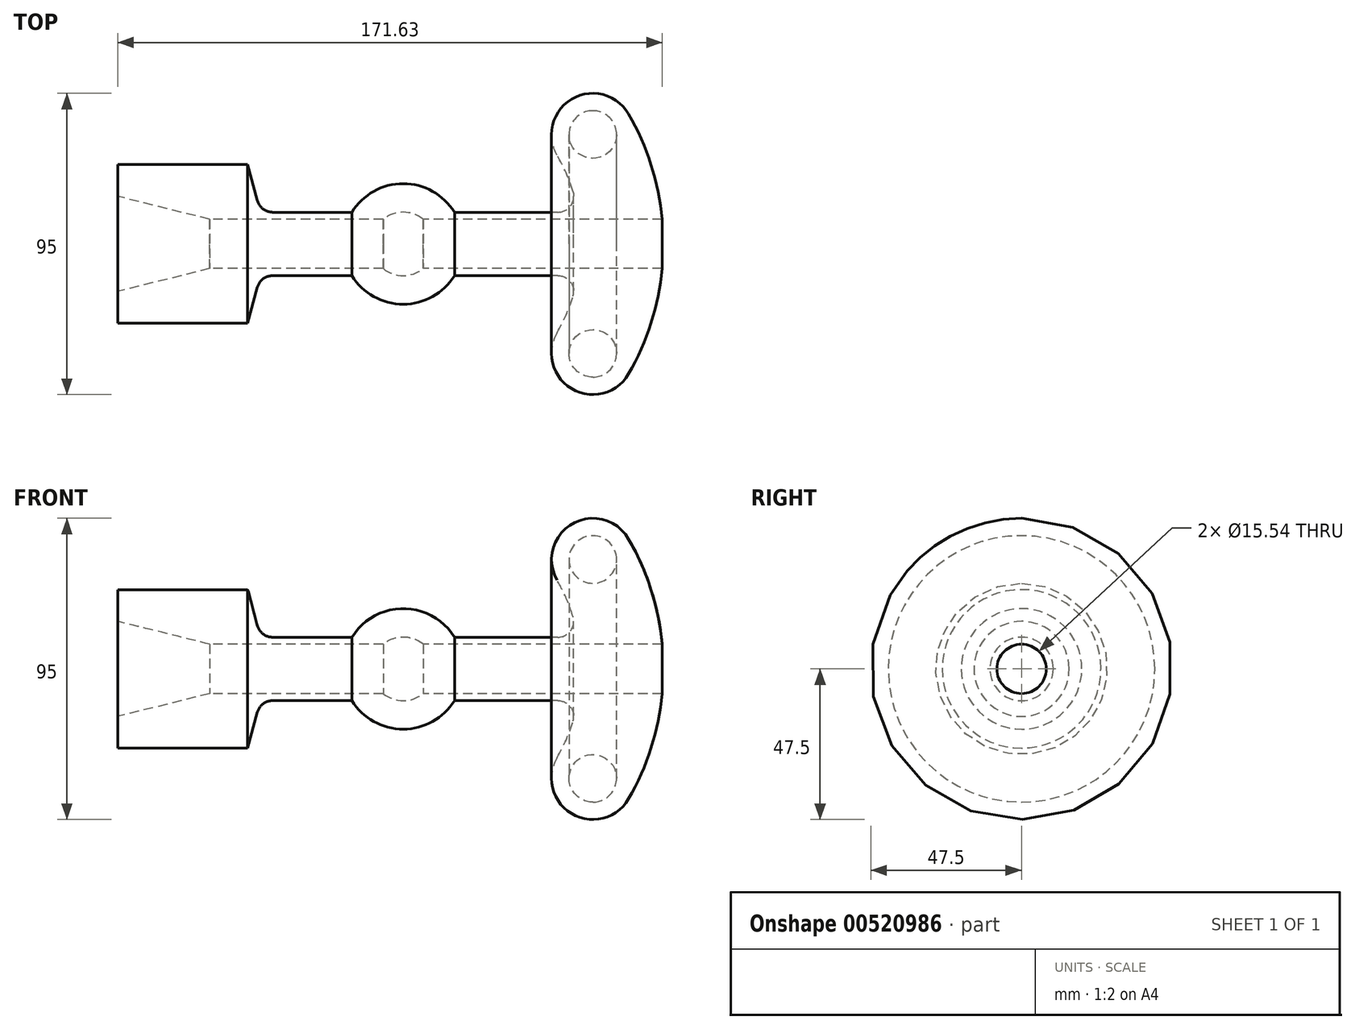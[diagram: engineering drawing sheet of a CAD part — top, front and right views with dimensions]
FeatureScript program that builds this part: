
annotation { "Feature Type Name" : "Feature", "Feature Type Description" : "" }
export const myFeature = defineFeature(function(context is Context, id is Id, definition is map)
    precondition{}
    {
        {
            var Q0;
            Q0=qCreatedBy(makeId("Front.planeOp"),FACE);
            var sketch = newSketch(context, id + "F0", { "sketchPlane" : qUnion([Q0])});
            skLineSegment(sketch, "E0", {"start": v(-90, 0) * mm, "end": v(69, 0) * mm, "construction": true});
            skArc(sketch, "E1", {"start": v(10, 0) * mm, "mid": v(0, 10) * mm, "end": v(-10, 0) * mm});
            skLineSegment(sketch, "E2", {"start": v(0, 0) * mm, "end": v(59.76, 34.5) * mm, "construction": true});
            skArc(sketch, "E3", {"start": v(69, 0) * mm, "mid": v(66.65, 17.86) * mm, "end": v(59.76, 34.5) * mm, "construction": true});
            skArc(sketch, "E4.0", {"start": v(82, 0) * mm, "mid": v(79.2, 21.22) * mm, "end": v(71.01, 41) * mm});
            skArc(sketch, "E5.0", {"start": v(55.1, 10) * mm, "mid": v(52.57, 19.28) * mm, "end": v(48.5, 28) * mm});
            skArc(sketch, "E6", {"start": v(71.01, 41) * mm, "mid": v(53.26, 45.76) * mm, "end": v(48.5, 28) * mm});
            skCircle(sketch, "E7", {"center": v(59.76, 34.5) * mm, "radius": 7.5 * mm});
            skLineSegment(sketch, "E8", {"start": v(0, 0) * mm, "end": v(56, 0) * mm, "construction": true});
            skArc(sketch, "E9", {"start": v(16.16, 10) * mm, "mid": v(0, 19) * mm, "end": v(-16.16, 10) * mm});
            skLineSegment(sketch, "E10.trimOffspring", {"start": v(16.16, 10) * mm, "end": v(55.1, 10) * mm});
            skLineSegment(sketch, "E11", {"start": v(-90, 25) * mm, "end": v(-90, 15) * mm});
            skLineSegment(sketch, "E12", {"start": v(-90, 25) * mm, "end": v(-49, 25) * mm});
            skLineSegment(sketch, "E13", {"start": v(-90, 15) * mm, "end": v(-61, 7.77) * mm});
            skLineSegment(sketch, "E14", {"start": v(0, 0) * mm, "end": v(-61, 0) * mm, "construction": true});
            skLineSegment(sketch, "E15", {"start": v(-61, 0) * mm, "end": v(-61, 7.77) * mm});
            skPoint(sketch, "E16.orphan", {"position": v(-90, 10) * mm});
            skLineSegment(sketch, "E17", {"start": v(-49, 25) * mm, "end": v(-44.98, 10) * mm});
            skLineSegment(sketch, "E18", {"start": v(-16.16, 10) * mm, "end": v(-44.98, 10) * mm});
            skLineSegment(sketch, "E19", {"start": v(-61, 0) * mm, "end": v(82, 0) * mm});
            skSolve(sketch);
        }
        {
            var Q0;
            {var subQ0=sQuery(id+"F0.wireOp",EDGE,"E1");Q0=makeQuery(id+"F0.imprint","IMPRINT",FACE,{"disambiguationData":[TD([[makeQuery(id+"F0.imprint","IMPRINT",EDGE,{"derivedFrom":subQ0}),-1.0]])]});}
            var Q1;
            Q1=sQuery(id+"F0.wireOp",EDGE,"E0");
            revolve(context, id + "F1", {"entities" : qUnion([Q0]), "axis" : qUnion([Q1]), "revolveType" : RevolveType.FULL});
        }
        {
            var Q0;
            Q0=makeQuery(id+"F1.opRevolve","SWEPT_EDGE",EDGE,{"disambiguationData":[OSD([sQuery(id+"F0.wireOp",EDGE,"E17"),sQuery(id+"F0.wireOp",EDGE,"E18")])]});
            var Q1;
            Q1=makeQuery(id+"F1.opRevolve","SWEPT_EDGE",EDGE,{"disambiguationData":[OSD([sQuery(id+"F0.wireOp",EDGE,"E5.0"),sQuery(id+"F0.wireOp",EDGE,"E10.trimOffspring")])]});
            fillet(context, id + "F2", {"entities" : qUnion([Q0, Q1]), "radius" : 5 * mm, "tangentPropagation" : true, "allowEdgeOverflow" : false});
        }
        {
            var Q0;
            Q0=makeQuery(id+"F1.opRevolve","SWEPT_FACE",FACE,{"disambiguationData":[OSD([sQuery(id+"F0.wireOp",EDGE,"E15")])]});
            extrude(context, id + "F3", {"entities" : qUnion([Q0]), "operationType" : NewBodyOperationType.REMOVE, "endBound" : BoundingType.THROUGH_ALL, "oppositeDirection" : true, "depth" : 25 * mm, "offsetDistance" : 25 * mm});
        }
    });
